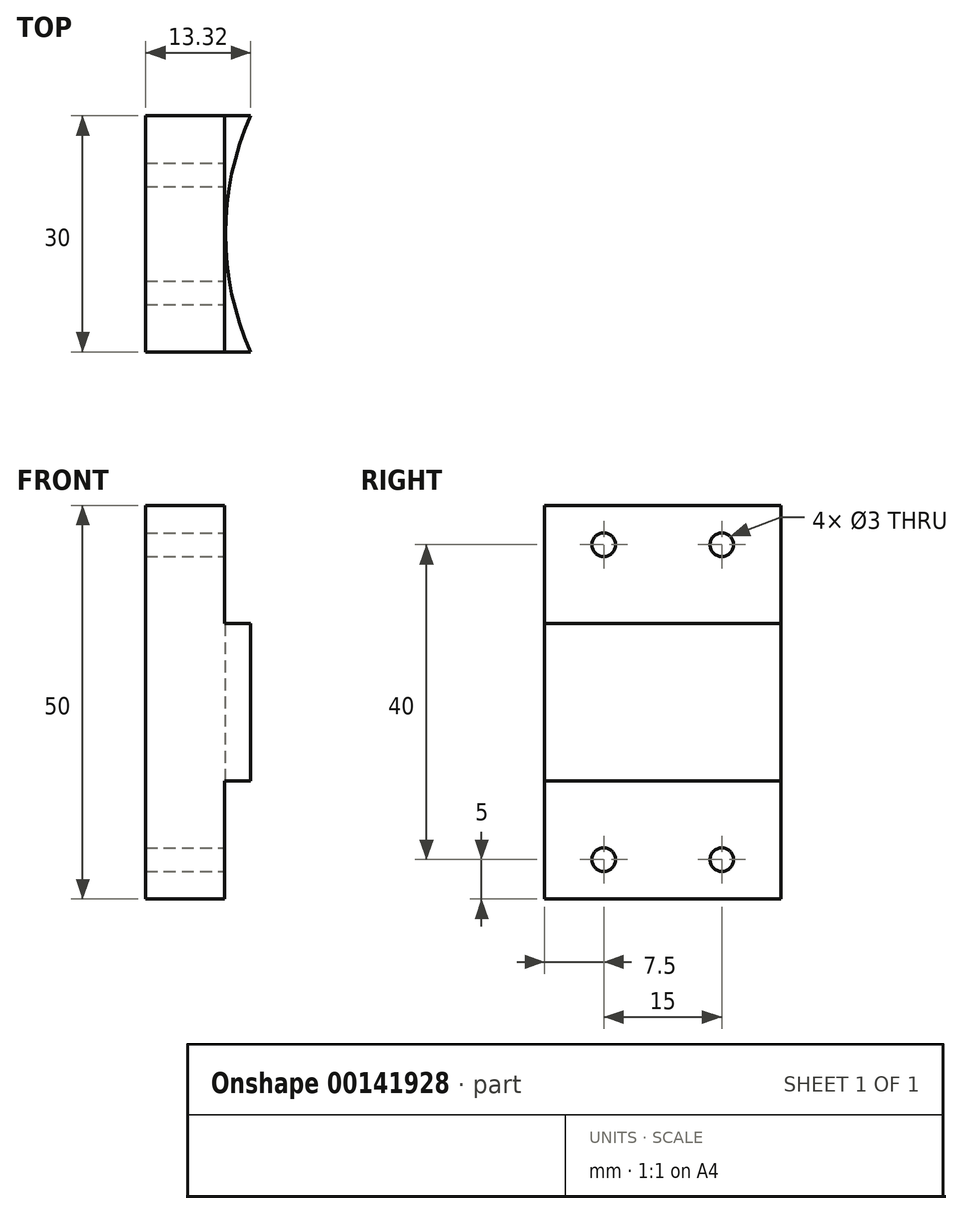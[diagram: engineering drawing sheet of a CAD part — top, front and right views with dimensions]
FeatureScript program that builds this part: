
annotation { "Feature Type Name" : "Feature", "Feature Type Description" : "" }
export const myFeature = defineFeature(function(context is Context, id is Id, definition is map)
    precondition{}
    {
        {
            var Q0;
            Q0=qCreatedBy(makeId("Right.planeOp"),FACE);
            var sketch = newSketch(context, id + "F0", { "sketchPlane" : qUnion([Q0])});
            skLineSegment(sketch, "E0.bottom", {"start": v(15, 25) * mm, "end": v(-15, 25) * mm});
            skLineSegment(sketch, "E0.top", {"start": v(15, -25) * mm, "end": v(-15, -25) * mm});
            skLineSegment(sketch, "E0.left", {"start": v(15, 25) * mm, "end": v(15, -25) * mm});
            skLineSegment(sketch, "E0.right", {"start": v(-15, 25) * mm, "end": v(-15, -25) * mm});
            skPoint(sketch, "E0.middle", {"position": v(0, 0) * mm});
            skSolve(sketch);
        }
        {
            var Q0;
            Q0 = qSketchRegion(id + "F0", true);
            extrude(context, id + "F1", {"entities" : qUnion([Q0]), "depth" : 10 * mm});
        }
        {
            var Q0;
            Q0=makeQuery(id+"F1.opExtrude","CAP_FACE",FACE,{"disambiguationData":[OSD([sQuery(id+"F0.wireOp",EDGE,"E0.bottom"),sQuery(id+"F0.wireOp",EDGE,"E0.top"),sQuery(id+"F0.wireOp",EDGE,"E0.left"),sQuery(id+"F0.wireOp",EDGE,"E0.right")])],"isStart":false});
            var sketch = newSketch(context, id + "F2", { "sketchPlane" : qUnion([Q0])});
            skLineSegment(sketch, "E1.bottom", {"start": v(-15, 10) * mm, "end": v(15, 10) * mm});
            skLineSegment(sketch, "E1.top", {"start": v(-15, -10) * mm, "end": v(15, -10) * mm});
            skLineSegment(sketch, "E1.left", {"start": v(-15, 10) * mm, "end": v(-15, -10) * mm});
            skLineSegment(sketch, "E1.right", {"start": v(15, 10) * mm, "end": v(15, -10) * mm});
            skPoint(sketch, "E1.middle", {"position": v(0, 0) * mm});
            skSolve(sketch);
        }
        {
            var Q0;
            Q0 = qSketchRegion(id + "F2", true);
            extrude(context, id + "F3", {"entities" : qUnion([Q0]), "operationType" : NewBodyOperationType.ADD, "depth" : 10 * mm});
        }
        {
            var Q0;
            Q0=qCreatedBy(makeId("Top.planeOp"),FACE);
            var sketch = newSketch(context, id + "F4", { "sketchPlane" : qUnion([Q0])});
            skCircle(sketch, "E2", {"center": v(47.14, 0) * mm, "radius": 37 * mm});
            skSolve(sketch);
        }
        {
            var Q0;
            Q0=makeQuery(id+"F4.imprint","IMPRINT",FACE,{"disambiguationData":[TD([[makeQuery(id+"F4.imprint","IMPRINT",EDGE,{"derivedFrom":sQuery(id+"F4.wireOp",EDGE,"E2")}),1.0]])]});
            extrude(context, id + "F5", {"entities" : qUnion([Q0]), "operationType" : NewBodyOperationType.REMOVE, "endBound" : BoundingType.THROUGH_ALL, "oppositeDirection" : true, "depth" : 25 * mm});
        }
        {
            var Q0;
            Q0 = qSketchRegion(id + "F4", true);
            extrude(context, id + "F6", {"entities" : qUnion([Q0]), "operationType" : NewBodyOperationType.REMOVE, "endBound" : BoundingType.THROUGH_ALL, "depth" : 25 * mm});
        }
        {
            var Q0;
            {var subQ0=sQuery(id+"F0.wireOp",EDGE,"E0.right");var subQ1=sQuery(id+"F0.wireOp",EDGE,"E0.left");var subQ2=sQuery(id+"F0.wireOp",EDGE,"E0.bottom");Q0=makeQuery(id+"F3.boolean.opBoolean","SPLIT",FACE,{"disambiguationData":[TD([makeQuery(id+"F1.opExtrude","SWEPT_FACE",FACE,{"disambiguationData":[OSD([subQ2])]})])],"derivedFrom":makeQuery(id+"F1.opExtrude","CAP_FACE",FACE,{"disambiguationData":[OSD([subQ2,sQuery(id+"F0.wireOp",EDGE,"E0.top"),subQ1,subQ0])],"isStart":false})});}
            var sketch = newSketch(context, id + "F7", { "sketchPlane" : qUnion([Q0])});
            skCircle(sketch, "E3", {"center": v(-7.5, 20) * mm, "radius": 1.5 * mm});
            skCircle(sketch, "E4", {"center": v(7.5, 20) * mm, "radius": 1.5 * mm});
            skCircle(sketch, "E5", {"center": v(-7.5, -20) * mm, "radius": 1.5 * mm});
            skCircle(sketch, "E6", {"center": v(7.5, -20) * mm, "radius": 1.5 * mm});
            skSolve(sketch);
        }
        {
            var Q0;
            Q0 = qSketchRegion(id + "F7", true);
            extrude(context, id + "F8", {"entities" : qUnion([Q0]), "operationType" : NewBodyOperationType.REMOVE, "endBound" : BoundingType.THROUGH_ALL, "oppositeDirection" : true, "depth" : 25 * mm});
        }
    });
